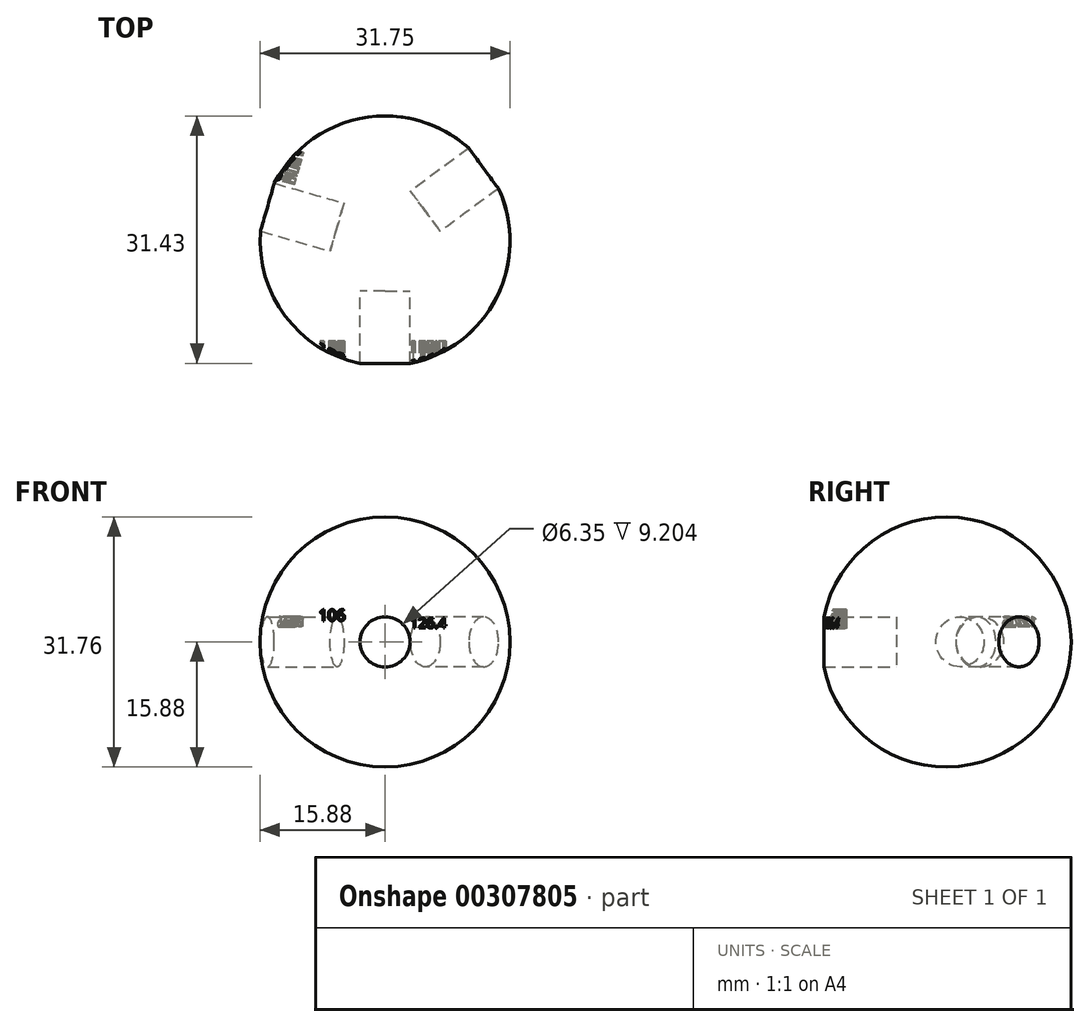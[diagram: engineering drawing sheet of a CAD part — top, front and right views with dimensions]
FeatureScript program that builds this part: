
annotation { "Feature Type Name" : "Feature", "Feature Type Description" : "" }
export const myFeature = defineFeature(function(context is Context, id is Id, definition is map)
    precondition{}
    {
        {
            var Q0;
            Q0=qCreatedBy(makeId("Front.planeOp"),FACE);
            var sketch = newSketch(context, id + "F0", { "sketchPlane" : qUnion([Q0])});
            skLineSegment(sketch, "E0", {"start": v(0, 0) * mm, "end": v(0, 73.37) * mm, "construction": true});
            skSolve(sketch);
        }
        {
            var Q0;
            Q0=qCreatedBy(makeId("Top.planeOp"),FACE);
            var sketch = newSketch(context, id + "F1", { "sketchPlane" : qUnion([Q0])});
            skArc(sketch, "E1", {"start": v(0, 15.88) * mm, "mid": v(-15.88, 0) * mm, "end": v(0, -15.88) * mm});
            skLineSegment(sketch, "E2", {"start": v(0, 15.88) * mm, "end": v(0, -15.88) * mm});
            skSolve(sketch);
        }
        {
            var Q0;
            Q0=makeQuery(id+"F1.imprint","IMPRINT",FACE,{"disambiguationData":[TD([[makeQuery(id+"F1.imprint","IMPRINT",EDGE,{"derivedFrom":sQuery(id+"F1.wireOp",EDGE,"E1")}),1.0]])]});
            var Q1;
            Q1=sQuery(id+"F1.wireOp",EDGE,"E2");
            revolve(context, id + "F2", {"entities" : qUnion([Q0]), "axis" : qUnion([Q1]), "revolveType" : RevolveType.FULL});
        }
        {
            var Q0;
            Q0=qCreatedBy(makeId("Front.planeOp"),FACE);
            cPlane(context, id + "F3", {"entities" : qUnion([Q0]), "cplaneType" : CPlaneType.OFFSET, "offset" : 6.35 * mm, "width" : 152.4 * mm, "height" : 152.4 * mm});
        }
        {
            var Q0;
            Q0=qCreatedBy(id+"F3.planeOp",FACE);
            var sketch = newSketch(context, id + "F4", { "sketchPlane" : qUnion([Q0])});
            skCircle(sketch, "E3", {"center": v(0, 0) * mm, "radius": 3.18 * mm});
            skSolve(sketch);
        }
        {
            var Q0;
            Q0 = qSketchRegion(id + "F4", true);
            extrude(context, id + "F5", {"entities" : qUnion([Q0]), "depth" : 25.4 * mm});
        }
        {
            var Q0;
            Q0=makeQuery(id+"F5.opExtrude","SWEPT_BODY",BODY,{"disambiguationData":[OSD([sQuery(id+"F4.wireOp",EDGE,"E3")])]});
            var Q1;
            Q1=sQuery(id+"F0.wireOp",EDGE,"E0");
            transform(context, id + "F6", {"entities" : qUnion([Q0]), "transformType" : TransformType.ROTATION, "transformAxis" : qUnion([Q1]), "angle" : 106 * degree, "oppositeDirection" : true, "makeCopy" : true});
        }
        {
            var Q0;
            Q0=makeQuery(id+"F6.opPattern","COPY",BODY,{"derivedFrom":makeQuery(id+"F5.opExtrude","SWEPT_BODY",BODY,{"disambiguationData":[OSD([sQuery(id+"F4.wireOp",EDGE,"E3")])]}),"instanceName":"1"});
            var Q1;
            Q1=sQuery(id+"F0.wireOp",EDGE,"E0");
            transform(context, id + "F7", {"entities" : qUnion([Q0]), "transformType" : TransformType.ROTATION, "transformAxis" : qUnion([Q1]), "angle" : 127.6 * degree, "oppositeDirection" : true, "makeCopy" : true});
        }
        {
            var Q0;
            Q0=makeQuery(id+"F5.opExtrude","CAP_FACE",FACE,{"disambiguationData":[OSD([sQuery(id+"F4.wireOp",EDGE,"E3")])],"isStart":false});
            cPlane(context, id + "F8", {"entities" : qUnion([Q0]), "cplaneType" : CPlaneType.OFFSET, "offset" : 12.7 * mm, "oppositeDirection" : true, "width" : 152.4 * mm, "height" : 152.4 * mm});
        }
        {
            var Q0;
            Q0=qCreatedBy(id+"F8.planeOp",FACE);
            var sketch = newSketch(context, id + "F9", { "sketchPlane" : qUnion([Q0])});
            skText(sketch, "E4", { "text": "106", "fontName": "OpenSans-Regular.ttf"});
            skText(sketch, "E5", { "text": "126.4", "fontName": "OpenSans-Regular.ttf"});
            const initialGuessF9  = {"E4": [-0.00843, 0.00269, 1, 0, 0.00142], "E5": [0.00317, 0.00176, 1, 0, 0.0013]};
            skSetInitialGuess(sketch, initialGuessF9);
            skSolve(sketch);
        }
        {
            var Q0;
            Q0 = qSketchRegion(id + "F9", true);
            extrude(context, id + "F10", {"entities" : qUnion([Q0]), "operationType" : NewBodyOperationType.REMOVE, "oppositeDirection" : true, "depth" : 6.35 * mm});
        }
        {
            var Q0;
            Q0=makeQuery(id+"F6.opPattern","COPY",FACE,{"derivedFrom":makeQuery(id+"F5.opExtrude","CAP_FACE",FACE,{"disambiguationData":[OSD([sQuery(id+"F4.wireOp",EDGE,"E3")])],"isStart":false}),"instanceName":"1"});
            cPlane(context, id + "F11", {"entities" : qUnion([Q0]), "cplaneType" : CPlaneType.OFFSET, "offset" : 12.7 * mm, "oppositeDirection" : true, "width" : 152.4 * mm, "height" : 152.4 * mm});
        }
        {
            var Q0;
            Q0=qCreatedBy(id+"F11.planeOp",FACE);
            var sketch = newSketch(context, id + "F12", { "sketchPlane" : qUnion([Q0])});
            skText(sketch, "E6", { "text": "127.6", "fontName": "OpenSans-Regular.ttf"});
            const initialGuessF12  = {"E6": [-0.00811, 0.00194, 1, 0, 0.00127]};
            skSetInitialGuess(sketch, initialGuessF12);
            skSolve(sketch);
        }
        {
            var Q0;
            Q0 = qSketchRegion(id + "F12", true);
            extrude(context, id + "F13", {"entities" : qUnion([Q0]), "operationType" : NewBodyOperationType.REMOVE, "oppositeDirection" : true, "depth" : 5.97 * mm});
        }
        {
            var Q0;
            Q0=makeQuery(id+"F5.opExtrude","SWEPT_BODY",BODY,{"disambiguationData":[OSD([sQuery(id+"F4.wireOp",EDGE,"E3")])]});
            var Q1;
            Q1=makeQuery(id+"F7.opPattern","COPY",BODY,{"derivedFrom":makeQuery(id+"F6.opPattern","COPY",BODY,{"derivedFrom":makeQuery(id+"F5.opExtrude","SWEPT_BODY",BODY,{"disambiguationData":[OSD([sQuery(id+"F4.wireOp",EDGE,"E3")])]}),"instanceName":"1"}),"instanceName":"1"});
            var Q2;
            Q2=makeQuery(id+"F6.opPattern","COPY",BODY,{"derivedFrom":makeQuery(id+"F5.opExtrude","SWEPT_BODY",BODY,{"disambiguationData":[OSD([sQuery(id+"F4.wireOp",EDGE,"E3")])]}),"instanceName":"1"});
            var Q3;
            Q3=makeQuery(id+"F2.opRevolve","SWEPT_BODY",BODY,{"disambiguationData":[OSD([sQuery(id+"F1.wireOp",EDGE,"E1"),sQuery(id+"F1.wireOp",EDGE,"E2")])]});
            booleanBodies(context, id + "F14", {"operationType" : BooleanOperationType.SUBTRACTION, "tools" : qUnion([Q0, Q1, Q2]), "targets" : qUnion([Q3])});
        }
    });
